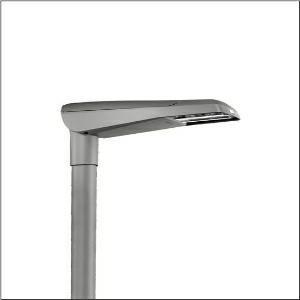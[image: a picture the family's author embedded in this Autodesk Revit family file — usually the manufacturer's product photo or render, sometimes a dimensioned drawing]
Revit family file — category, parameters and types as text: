
# Revit family: streetlight_sl_11_iq_micro___st1_2a_5xc1a41e08ce_a543
name_source: partatom
category: Lighting Fixtures
units: mm (PartAtom-declared; Revit-internal decimal feet)

## family parameters
Cut with Voids When Loaded = No
Host = Face
Light Source = No
Part Type = Normal
Room Calculation Point = No
Round Connector Dimension = Use Diameter
Shared = No

## types (1)
- --- (1 x LED, 1960 lm, 12.6 W, 4000K)
    Apparent Load = 13 VA
    CIE Flux Codes = 33 71 96 100 100
    Color Rendering = 70
    Color Temperature = 4000K
    Default Elevation = 1800 mm
    Description = Streetlight SL 11 iQ micro, mast luminaire, primary light control with 3 zone facetted reflector, of plastic, silver coated, highly specular, primary optical cover: cover, of PMMA, transparent, light distribution: ST1.2a, light emission: direct distribution, primary light characteristic: asymmetric, installation type: post-top, side-entry, lamps: LED, High Power LED, rated values: 1.960lm | 12,6W | 155,6lm/W (begin service life); end service life: 1.960lm | 12,9W; at 50% lumin. flux: 980lm | 6,8W | 144,1lm/W, colour temperature: 4000K, colour rendering: CRI > 70, light colour: 740, light setting 1 begin service life: 100% | 1.960lm | 12,6W | 155,6lm/W | 4.000K, light setting 1 end service life: 12,9W, further light settings possible, control: optimised constant luminous flux control (CLO 2.0), Desk-Remote (wireless, voltage-free reading and setting of iQ features in the workshop via application-optimized NFC function/RFID function), Light-Fading, Smart-Wire, Night-Set, Lumen-Switch, Temp-Guard, Auto-Match, with cable H07RN-F 5x 1.5mm², mains connection: 230..240V, AC, 50/60Hz, connection cable pre-assembled, cable length: 5,5m, luminaire housing, of diecast aluminium, powder-coated, Siteco® metallic grey (DB 702S), please order mast flange separately, inclination adjustable without tools: 0°, 5°, 10°, 15° (post-top) | 0°, -5°, -10°, -15° (side-entry), sealing non-destructively replaceable, multi-level sealing system, length: 600mm, width: 174mm, height: 116mm, mast flange for spigot size: 42mm (side-entry): 5XC10008XM4, 60/48mm (side-entry/post-top): 5XC10108XM2, 76/60mm (side-entry/post-top): 5XC10108XM1, equipment: standard, protection rating (complete): IP66, insulation class (complete): insulation class II (safety insulation), certification: CE, ENEC, ENEC+, VDE, impact resistance: IK10, permissible operating ambient temperature for outdoor applications: -25..+50°C, standard-compliant lighting for roads and squares, Environmental Product Declaration (EPD) tested and certified by an independent institute, packaging unit: 1 piece

Light Distribution: ST1.2a
    Height = 116 mm
    Lamp = 1 x LED
    Lamp Light Flux = 1960 lm
    Lamp Power = 12.6 W
    Lamp count = 1
    Length = 600 mm
    Luminous efficacy = 156 lm/W
    Manufacturer = Siteco
    ModVariant = No
    Model = 5XC1A41E08CE
    Number of Poles = 1
    OnlyDefault = Yes
    Power Factor = 1
    Product Name = Streetlight SL 11 iQ micro | ST1.2a
    Product group = mast luminaire | pylon top
    ProductGroupID = 6100
    Protection Class = Protection class II
    Protection Degree = IP 66
    RLX_Detail_Level = 1
    RLX_Emergency_Light_Flux = 0 lm
    RLX_Emergency_Type = 0
    RLX_Emergency_Type_DB = No
    RlxData = <blob elided: 26501 chars, md5=e670a1aa>
    Socket = socket
    Standby Power = 0 W
    System Light Flux = 1960 lm
    System Power = 13 W
    Type Comments = factory setting: luminous flux: 100 % | dim-lin: 254 | 229 mA
    Type Image = l_1006566.jpg
    URL = http://relux.com
    VarID = @adj_018115
    Voltage = 0 V
    Weight = 0.00 kg
    Width = 174 mm

## geometry (parser evidence)
native form markers: Blend x4, Sweep x11
no freeform markers — native parametric forms only
